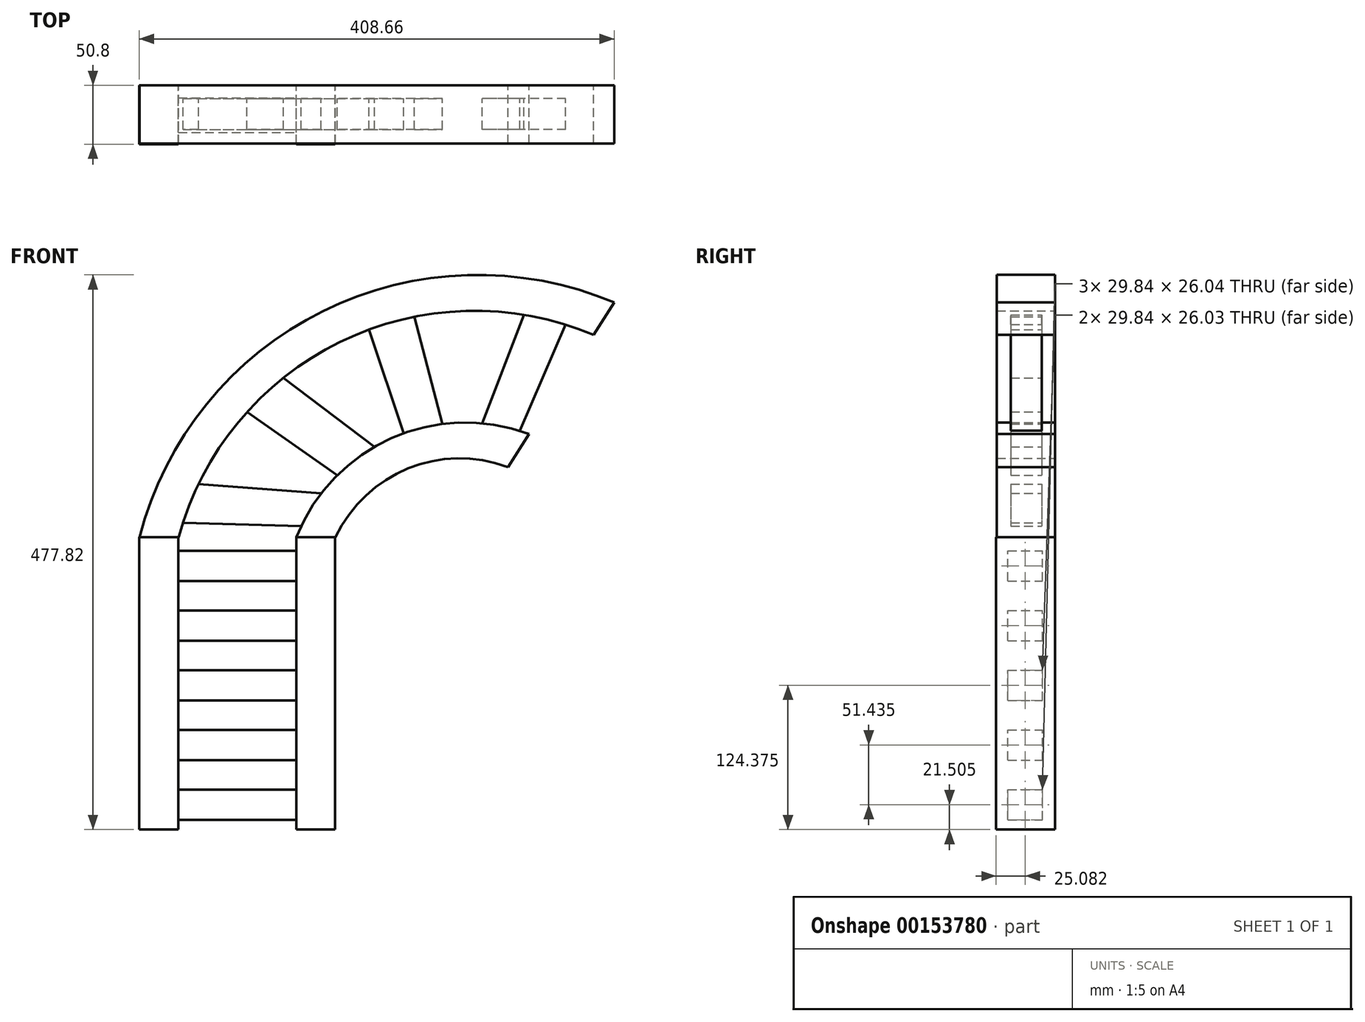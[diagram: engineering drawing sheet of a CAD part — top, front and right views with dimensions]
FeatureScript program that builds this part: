
annotation { "Feature Type Name" : "Feature", "Feature Type Description" : "" }
export const myFeature = defineFeature(function(context is Context, id is Id, definition is map)
    precondition{}
    {
        {
            var Q0;
            Q0=qCreatedBy(makeId("Front.planeOp"),FACE);
            var sketch = newSketch(context, id + "F0", { "sketchPlane" : qUnion([Q0])});
            skLineSegment(sketch, "E0.bottom", {"start": v(-91.03, -95.5) * mm, "end": v(-57.46, -95.5) * mm});
            skLineSegment(sketch, "E0.top", {"start": v(-91.03, 156.28) * mm, "end": v(-57.46, 156.28) * mm});
            skLineSegment(sketch, "E0.left", {"start": v(-91.03, -95.5) * mm, "end": v(-91.03, 156.28) * mm});
            skLineSegment(sketch, "E0.right", {"start": v(-57.46, -95.5) * mm, "end": v(-57.46, 156.28) * mm});
            skLineSegment(sketch, "E1.bottom", {"start": v(44.14, -95.5) * mm, "end": v(77.55, -95.5) * mm});
            skLineSegment(sketch, "E1.top", {"start": v(44.14, 156.28) * mm, "end": v(77.55, 156.28) * mm});
            skLineSegment(sketch, "E1.left", {"start": v(44.14, -95.5) * mm, "end": v(44.14, 156.28) * mm});
            skLineSegment(sketch, "E1.right", {"start": v(77.55, -95.5) * mm, "end": v(77.55, 156.28) * mm});
            skSolve(sketch);
        }
        {
            var Q0;
            Q0 = qSketchRegion(id + "F0", true);
            extrude(context, id + "F1", {"entities" : qUnion([Q0]), "depth" : 50.8 * mm});
        }
        {
            var Q0;
            Q0=qCreatedBy(makeId("Front.planeOp"),FACE);
            var sketch = newSketch(context, id + "F2", { "sketchPlane" : qUnion([Q0])});
            skLineSegment(sketch, "E2.bottom", {"start": v(-57.93, -87.01) * mm, "end": v(44.5, -87.01) * mm});
            skLineSegment(sketch, "E2.top", {"start": v(-57.93, -60.98) * mm, "end": v(44.5, -60.98) * mm});
            skLineSegment(sketch, "E2.left", {"start": v(-57.93, -87.01) * mm, "end": v(-57.93, -60.98) * mm});
            skLineSegment(sketch, "E2.right", {"start": v(44.5, -87.01) * mm, "end": v(44.5, -60.98) * mm});
            skLineSegment(sketch, "E3.bottom", {"start": v(-57.93, -35.58) * mm, "end": v(44.5, -35.58) * mm});
            skLineSegment(sketch, "E3.top", {"start": v(-57.93, -9.54) * mm, "end": v(44.5, -9.54) * mm});
            skLineSegment(sketch, "E3.left", {"start": v(-57.93, -35.58) * mm, "end": v(-57.93, -9.54) * mm});
            skLineSegment(sketch, "E3.right", {"start": v(44.5, -35.58) * mm, "end": v(44.5, -9.54) * mm});
            skLineSegment(sketch, "E4.bottom", {"start": v(-57.93, 15.86) * mm, "end": v(44.5, 15.86) * mm});
            skLineSegment(sketch, "E4.top", {"start": v(-57.93, 41.9) * mm, "end": v(44.5, 41.9) * mm});
            skLineSegment(sketch, "E4.left", {"start": v(-57.93, 15.86) * mm, "end": v(-57.93, 41.9) * mm});
            skLineSegment(sketch, "E4.right", {"start": v(44.5, 15.86) * mm, "end": v(44.5, 41.9) * mm});
            skLineSegment(sketch, "E5.bottom", {"start": v(-57.93, 67.3) * mm, "end": v(44.5, 67.3) * mm});
            skLineSegment(sketch, "E5.top", {"start": v(-57.93, 93.33) * mm, "end": v(44.5, 93.33) * mm});
            skLineSegment(sketch, "E5.left", {"start": v(-57.93, 67.3) * mm, "end": v(-57.93, 93.33) * mm});
            skLineSegment(sketch, "E5.right", {"start": v(44.5, 67.3) * mm, "end": v(44.5, 93.33) * mm});
            skLineSegment(sketch, "E6.bottom", {"start": v(-57.93, 118.73) * mm, "end": v(44.5, 118.73) * mm});
            skLineSegment(sketch, "E6.top", {"start": v(-57.93, 144.76) * mm, "end": v(44.5, 144.76) * mm});
            skLineSegment(sketch, "E6.left", {"start": v(-57.93, 118.73) * mm, "end": v(-57.93, 144.76) * mm});
            skLineSegment(sketch, "E6.right", {"start": v(44.5, 118.73) * mm, "end": v(44.5, 144.76) * mm});
            skSolve(sketch);
        }
        {
            var Q0;
            Q0 = qSketchRegion(id + "F2", true);
            extrude(context, id + "F3", {"entities" : qUnion([Q0]), "operationType" : NewBodyOperationType.ADD, "depth" : 40.64 * mm, "hasSecondDirection" : true, "secondDirectionOppositeDirection" : false, "secondDirectionDepth" : 10.8 * mm});
        }
        {
            var Q0;
            Q0=makeQuery(id+"F1.opExtrude","SWEPT_BODY",BODY,{"disambiguationData":[OSD([sQuery(id+"F0.wireOp",EDGE,"E0.bottom"),sQuery(id+"F0.wireOp",EDGE,"E0.top"),sQuery(id+"F0.wireOp",EDGE,"E0.left"),sQuery(id+"F0.wireOp",EDGE,"E0.right")])]});
            var Q1;
            Q1=qCreatedBy(makeId("Right.planeOp"),FACE);
            mirror(context, id + "F4", {"entities" : qUnion([Q0]), "mirrorPlane" : qUnion([Q1])});
        }
        {
            var Q0;
            Q0=makeQuery(id+"F1.opExtrude","SWEPT_BODY",BODY,{"disambiguationData":[OSD([sQuery(id+"F0.wireOp",EDGE,"E0.bottom"),sQuery(id+"F0.wireOp",EDGE,"E0.top"),sQuery(id+"F0.wireOp",EDGE,"E0.left"),sQuery(id+"F0.wireOp",EDGE,"E0.right")])]});
            var Q1;
            Q1=qCreatedBy(makeId("Top.planeOp"),FACE);
            mirror(context, id + "F5", {"entities" : qUnion([Q0]), "mirrorPlane" : qUnion([Q1])});
        }
        {
            var Q0;
            Q0=makeQuery(id+"F1.opExtrude","SWEPT_BODY",BODY,{"disambiguationData":[OSD([sQuery(id+"F0.wireOp",EDGE,"E0.bottom"),sQuery(id+"F0.wireOp",EDGE,"E0.top"),sQuery(id+"F0.wireOp",EDGE,"E0.left"),sQuery(id+"F0.wireOp",EDGE,"E0.right")])]});
            var Q1;
            Q1=qCreatedBy(makeId("Right.planeOp"),FACE);
            mirror(context, id + "F6", {"entities" : qUnion([Q0]), "mirrorPlane" : qUnion([Q1])});
        }
        {
            var Q0;
            Q0=makeQuery(id+"F6.opPattern","COPY",BODY,{"derivedFrom":makeQuery(id+"F1.opExtrude","SWEPT_BODY",BODY,{"disambiguationData":[OSD([sQuery(id+"F0.wireOp",EDGE,"E0.bottom"),sQuery(id+"F0.wireOp",EDGE,"E0.top"),sQuery(id+"F0.wireOp",EDGE,"E0.left"),sQuery(id+"F0.wireOp",EDGE,"E0.right")])]}),"instanceName":"1"});
            deleteBodies(context, id + "F7", {"entities" : qUnion([Q0])});
        }
        {
            var Q0;
            Q0=makeQuery(id+"F5.opPattern","COPY",BODY,{"derivedFrom":makeQuery(id+"F1.opExtrude","SWEPT_BODY",BODY,{"disambiguationData":[OSD([sQuery(id+"F0.wireOp",EDGE,"E0.bottom"),sQuery(id+"F0.wireOp",EDGE,"E0.top"),sQuery(id+"F0.wireOp",EDGE,"E0.left"),sQuery(id+"F0.wireOp",EDGE,"E0.right")])]}),"instanceName":"1"});
            deleteBodies(context, id + "F8", {"entities" : qUnion([Q0])});
        }
        {
            var Q0;
            Q0=makeQuery(id+"F4.opPattern","COPY",BODY,{"derivedFrom":makeQuery(id+"F1.opExtrude","SWEPT_BODY",BODY,{"disambiguationData":[OSD([sQuery(id+"F0.wireOp",EDGE,"E0.bottom"),sQuery(id+"F0.wireOp",EDGE,"E0.top"),sQuery(id+"F0.wireOp",EDGE,"E0.left"),sQuery(id+"F0.wireOp",EDGE,"E0.right")])]}),"instanceName":"1"});
            deleteBodies(context, id + "F9", {"entities" : qUnion([Q0])});
        }
        {
            var Q0;
            Q0=qCreatedBy(makeId("Front.planeOp"),FACE);
            var sketch = newSketch(context, id + "F10", { "sketchPlane" : qUnion([Q0])});
            skLineSegment(sketch, "E7", {"start": v(-90.93, 156.43) * mm, "end": v(-57.18, 156.43) * mm});
            skArc(sketch, "E8", {"start": v(317.63, 358.53) * mm, "mid": v(67.02, 351.13) * mm, "end": v(-90.93, 156.43) * mm});
            skArc(sketch, "E9", {"start": v(299.95, 330.76) * mm, "mid": v(81.84, 324.62) * mm, "end": v(-57.18, 156.43) * mm});
            skLineSegment(sketch, "E10", {"start": v(317.63, 358.53) * mm, "end": v(299.95, 330.76) * mm});
            skLineSegment(sketch, "E11", {"start": v(44.1, 156.43) * mm, "end": v(77.86, 156.43) * mm});
            skArc(sketch, "E12", {"start": v(244.3, 245.29) * mm, "mid": v(126.08, 241.68) * mm, "end": v(44.1, 156.43) * mm});
            skLineSegment(sketch, "E13", {"start": v(244.3, 245.29) * mm, "end": v(226.17, 216.79) * mm});
            skArc(sketch, "E14", {"start": v(226.17, 216.79) * mm, "mid": v(140.2, 215.61) * mm, "end": v(77.86, 156.43) * mm});
            skSolve(sketch);
        }
        {
            var Q0;
            Q0 = qSketchRegion(id + "F10", true);
            extrude(context, id + "F11", {"entities" : qUnion([Q0]), "depth" : 50.16 * mm});
        }
        {
            var Q0;
            Q0=qCreatedBy(makeId("Front.planeOp"),FACE);
            var sketch = newSketch(context, id + "F12", { "sketchPlane" : qUnion([Q0])});
            skLineSegment(sketch, "E15", {"start": v(-58.79, 169.05) * mm, "end": v(51.94, 165.92) * mm});
            skArc(sketch, "E16", {"start": v(-43.86, 202.37) * mm, "mid": v(-52.52, 186.25) * mm, "end": v(-58.79, 169.05) * mm});
            skLineSegment(sketch, "E17", {"start": v(-43.86, 202.37) * mm, "end": v(69.98, 193.7) * mm});
            skArc(sketch, "E18", {"start": v(51.94, 165.92) * mm, "mid": v(61.37, 179.54) * mm, "end": v(69.98, 193.7) * mm});
            skLineSegment(sketch, "E19", {"start": v(-3.25, 267.62) * mm, "end": v(82.83, 207.23) * mm});
            skArc(sketch, "E20", {"start": v(31.11, 295.04) * mm, "mid": v(11.47, 284.41) * mm, "end": v(-3.25, 267.62) * mm});
            skLineSegment(sketch, "E21", {"start": v(31.11, 295.04) * mm, "end": v(115.1, 231.18) * mm});
            skArc(sketch, "E22", {"start": v(82.83, 207.23) * mm, "mid": v(100.38, 217.3) * mm, "end": v(115.1, 231.18) * mm});
            skLineSegment(sketch, "E23", {"start": v(104.23, 342.23) * mm, "end": v(137.7, 242.57) * mm});
            skArc(sketch, "E24", {"start": v(143.94, 353.26) * mm, "mid": v(123.43, 350.1) * mm, "end": v(104.23, 342.23) * mm});
            skLineSegment(sketch, "E25", {"start": v(143.94, 353.26) * mm, "end": v(170.79, 249.56) * mm});
            skArc(sketch, "E26", {"start": v(137.7, 242.57) * mm, "mid": v(154.64, 244.17) * mm, "end": v(170.79, 249.56) * mm});
            skArc(sketch, "E27", {"start": v(279.48, 347.83) * mm, "mid": v(262.24, 354.81) * mm, "end": v(244.09, 358.84) * mm});
            skLineSegment(sketch, "E28", {"start": v(244.09, 358.84) * mm, "end": v(202.41, 249.93) * mm});
            skLineSegment(sketch, "E29", {"start": v(279.48, 347.83) * mm, "end": v(233.08, 240.46) * mm});
            skArc(sketch, "E30", {"start": v(202.41, 249.93) * mm, "mid": v(217.3, 243.75) * mm, "end": v(233.08, 240.46) * mm});
            skSolve(sketch);
        }
        {
            var Q0;
            Q0 = qSketchRegion(id + "F12", true);
            extrude(context, id + "F13", {"entities" : qUnion([Q0]), "operationType" : NewBodyOperationType.ADD, "depth" : 38.1 * mm, "hasSecondDirection" : true, "secondDirectionOppositeDirection" : false, "secondDirectionDepth" : 11.43 * mm});
        }
    });
